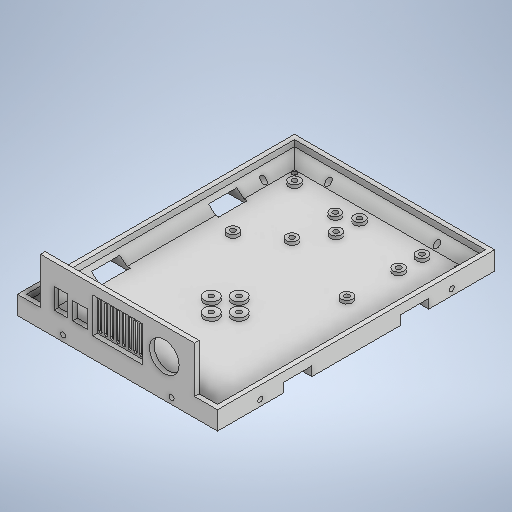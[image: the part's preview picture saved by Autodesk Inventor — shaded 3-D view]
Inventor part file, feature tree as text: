
AUTODESK INVENTOR PART (.ipt)
format: ipt  version: 2025.1 (Build 291241000, 241)  size: 726,016 bytes
history: native  units: mm
features: extrude x15, sketch x14, chamfer x2, imported_body x1
ambient origin geometry x8: Origin, YZ Plane, XZ Plane, XY Plane, X Axis, Y Axis, Z Axis, Center Point
bodies: Body1 (feature_tree)
feature tree (32):
  extrude  "Extrusión6"  Depth=180.0mm
  extrude  "Extrusión7"  Depth=3.0mm
  extrude  "Extrusión13"  Depth=6.0mm
  extrude  "Extrusión12"  Depth=54.0mm
  extrude  "Extrusión11"  Depth=3.0mm
  extrude  "Extrusión8"  Depth=3.0mm
  chamfer  "Chaflán1"  Distance=3.0mm
  extrude  "Extrusión16"  Depth=2.0mm
  extrude  "Extrusión14"  Depth=2.0mm
  extrude  "Extrusión9"  Depth=2.0mm
  extrude  "Extrusión10"  Depth=2.0mm
  extrude  "Extrusión15"  Depth=2.0mm
  extrude  "Extrusión17"  Depth=2.0mm
  extrude  "Extrusión18"  Depth=2.0mm
  chamfer  "Chaflán2"  Distance=18.0mm
  extrude  "Extrusión19"  Depth=2.0mm
  extrude  "Extrusión20"  Depth=6.0mm
  imported_body  "base"
  sketch  "Boceto10"  dims[d53=130.0mm d54=180.0mm]
  sketch  "Boceto11"  dims[d55=2.0mm d56=0.0mm d57=3.0mm]
  sketch  "Boceto12"  dims[d58=10.0mm d59=0.0mm d60=6.0mm]
  sketch  "Boceto13"  dims[d64=102.0mm d65=54.0mm]
  sketch  "Boceto15"  dims[d71=3.0mm d73=3.0mm]
  sketch  "Boceto16"  dims[d74=14.0mm d75=3.0mm]
  sketch  "Boceto17"  dims[d76=48.0mm]
  sketch  "Boceto18"  dims[d78=82.0mm]
  sketch  "Boceto19"  dims[d80=74.0mm]
  sketch  "Boceto20"  dims[d86=50.8mm]
  sketch  "Boceto21"  dims[d87=15.2mm]
  sketch  "Boceto22"  dims[d88=3.25mm]
  sketch  "Boceto23"  dims[d89=50.8mm]
  sketch  "Boceto24"  dims[d90=4.7mm d91=3.0mm d92=0.9mm d96=61.0mm d97=40.64mm d98=15.24mm d99=3.25mm d100=3.25mm d101=3.25mm d102=18.0mm d103=102.0mm d104=6.0mm d105=3.25mm d106=3.25mm d107=3.25mm d108=3.25mm d109=3.0mm d110=3.0mm d111=3.0mm d112=3.0mm d113=2.0mm d114=2.0mm d115=2.0mm d116=2.0mm d117=2.0mm d118=2.0mm d119=2.0mm d120=2.0mm d121=2.0mm d122=2.0mm d123=0.0mm d124=2.0mm d125=2.0mm d126=2.0mm d127=2.0mm d128=2.0mm d130=3.0mm d131=3.0mm d132=3.0mm d133=3.0mm d134=2.0mm d135=2.0mm d136=2.0mm d137=30.0mm d138=0.0mm d139=1.7mm d140=1.7mm d141=1.7mm d142=1.7mm d143=1.7mm d144=1.7mm d145=1.7mm d146=1.7mm d147=1.7mm d148=1.7mm d149=1.7mm d150=1.7mm d151=1.7mm d152=1.0mm d153=0.0mm d155=12.0mm d156=12.0mm d157=12.0mm d158=12.0mm d159=12.0mm d160=12.0mm d161=12.0mm d162=12.0mm d163=3.25mm d164=3.25mm d165=3.25mm d166=3.25mm d167=30.0mm d168=0.0mm d170=7.0mm d171=6.0mm d172=0.0mm d173=7.0mm d174=6.0mm d175=45.0deg d176=15.0mm d177=15.0mm d178=30.0mm d179=0.0mm d182=9.4mm d184=10.0mm d185=0.0mm d186=34.55mm d188=19.3mm d189=60.0mm d190=15.0mm d191=8.4mm d192=13.4mm d193=23.0mm d195=12.0mm d196=20.0mm d198=20.0mm d201=15.0mm d202=24.0mm d203=15.0mm d204=36.0mm d205=1.5mm d207=50.0mm d226=2.0mm d227=2.0mm d228=0.0mm d229=1.0mm d230=2.0mm d231=45.0deg d235=140.0mm d236=0.0mm d237=3.25mm d238=3.25mm d239=3.25mm d240=3.25mm d241=20.0mm d242=0.0mm d243=3.25mm d244=3.25mm d245=12.0mm d246=0.0mm d247=4.0mm d248=4.0mm d250=25.0mm d302=38.0mm d304=18.4mm d305=6.0mm d306=9.2mm d307=62.2mm d308=62.2mm d309=12.0mm d310=0.0mm d311=38.0mm d312=9.2mm d313=18.4mm d314=6.0mm d315=12.0mm d316=0.0mm d323=35.2mm d324=35.2mm d327=35.2mm d328=35.2mm d380=3.25mm d381=3.25mm d382=3.25mm d383=3.25mm d385=3.25mm d386=3.25mm d387=3.25mm d388=3.25mm d389=3.25mm d390=3.25mm d391=3.25mm d393=3.25mm d395=3.25mm d396=3.25mm d397=3.25mm d398=3.25mm d399=3.25mm d400=3.25mm d401=3.25mm d402=3.25mm d403=3.25mm d404=3.25mm d405=4.0mm d406=4.0mm d407=11.4mm d408=2.0mm d409=2.0mm d410=2.0mm d411=2.0mm d412=2.0mm d413=2.0mm d414=2.0mm d415=2.0mm d424=5.5mm d425=1.8mm d426=1.8mm d427=1.8mm d428=1.8mm d429=1.8mm d430=1.8mm d431=1.8mm]
